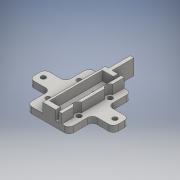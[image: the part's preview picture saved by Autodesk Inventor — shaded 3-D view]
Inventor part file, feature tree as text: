
AUTODESK INVENTOR PART (.ipt)
format: ipt  version: 2016 SP1 (Build 200210100, 210)  size: 358,912 bytes
history: native  units: mm
features: extrude x10, sketch x8, fillet x3, projected_geometry x2, hole x1
ambient origin geometry x8: Origin, YZ Plane, XZ Plane, XY Plane, X Axis, Y Axis, Z Axis, Center Point
bodies: Solid1 (feature_tree)
feature tree (24):
  extrude  "Extrusion1"  Depth=3.0mm
  extrude  "Extrusion2"  Depth=10.0mm
  extrude  "Extrusion3"  Depth=3.0mm
  extrude  "Extrusion4"  Depth=20.0mm
  extrude  "Extrusion5"  Depth=10.0mm
  hole  "Hole1"  [1 undecoded]
  fillet  "Fillet5"  Radius=40.0mm
  fillet  "Fillet7"  Radius=10.0mm
  extrude  "Extrusion7"  Depth=4.0mm
  fillet  "Fillet9"  Radius=6.0mm
  extrude  "Extrusion8"  Depth=10.0mm
  extrude  "Extrusion10"  Depth=15.0mm
  extrude  "Extrusion9"  Depth=2.0mm
  extrude  "Extrusion6"  Depth=2.0mm
  sketch  "Sketch3"  dims[d0=3.0mm d1=3.0mm]
  sketch  "Sketch4"  dims[d2=20.0mm d3=10.0mm]
  sketch  "Sketch5"  dims[d4=3.0mm d5=3.0mm]
  sketch  "Sketch9"  dims[d6=20.0mm d7=20.0mm]
  sketch  "Sketch11"  dims[d8=20.0mm d9=10.0mm]
  sketch  "Sketch12"  dims[d10=30.0mm d11=15.0mm d12=40.0mm d13=10.0mm]
  projected_geometry  "Projected Loop2"
  sketch  "Sketch13"  dims[d14=4.0mm d15=0.0mm d16=4.0mm d20=6.0mm d21=0.0mm]
  projected_geometry  "Projected Loop3"
  sketch  "Sketch14"  dims[d23=2.5mm d24=2.5mm d25=15.0mm d26=2.0mm d27=2.0mm d28=12.0mm d29=2.5mm d30=6.0mm d31=4.0mm d32=2.0mm d33=90.0deg d34=8.0mm d35=20.594885mm d36=6.3mm d37=5.5mm d38=5.5mm d39=8.0mm d40=0.0mm d47=8.0mm d48=0.0mm d77=10.0mm d78=40.0mm d79=15.0mm d80=3.0mm d81=3.0mm d82=46.0mm d83=54.0mm d84=23.0mm d85=27.0mm d86=8.0mm d87=0.0mm d90=8.0mm d91=0.0mm d94=1.0mm d96=0.0mm d97=0.0mm d110=2.0mm d111=0.7mm d112=3.0mm d115=3.0mm d116=1.3mm d117=2.0mm d118=2.0mm d119=2.0mm d121=27.0mm d122=13.5mm d123=10.0mm d124=0.0mm d125=3.0mm d126=3.0mm d128=6.0mm d129=3.0mm d130=10.0mm d131=0.0mm d132=3.0mm d133=21.0mm d134=4.0mm d135=2.0mm d136=10.5mm d137=10.0mm d138=0.0mm d139=0.0mm d140=0.0mm d141=22.0mm d142=14.0mm d143=1.2mm d144=1.2mm d145=10.0mm d146=0.0mm]
note: 1 required parameter value undecoded (feature->parameter linkage not recoverable at this tier; creation-order binding heuristic only, values carry confidence <= 0.55)
